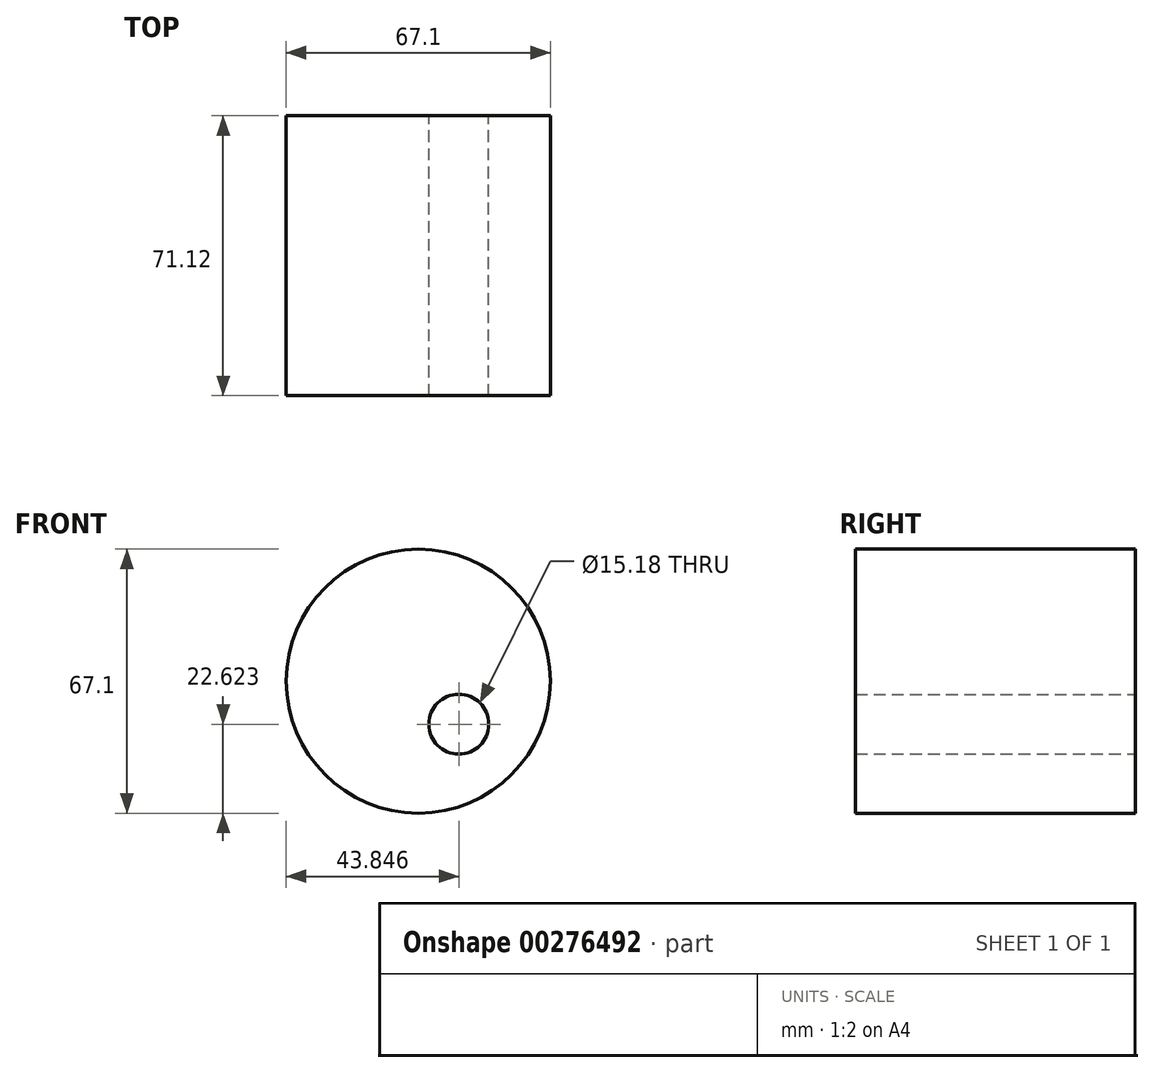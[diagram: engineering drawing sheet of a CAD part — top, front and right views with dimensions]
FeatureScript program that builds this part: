
annotation { "Feature Type Name" : "Feature", "Feature Type Description" : "" }
export const myFeature = defineFeature(function(context is Context, id is Id, definition is map)
    precondition{}
    {
        {
            var Q0;
            Q0=qCreatedBy(makeId("Front.planeOp"),FACE);
            var sketch = newSketch(context, id + "F0", { "sketchPlane" : qUnion([Q0])});
            skCircle(sketch, "E0", {"center": v(0, 0) * mm, "radius": 33.55 * mm});
            skCircle(sketch, "E1", {"center": v(10.3, -10.93) * mm, "radius": 7.6 * mm});
            skSolve(sketch);
        }
        {
            var Q0;
            Q0 = qSketchRegion(id + "F0", true);
            extrude(context, id + "F1", {"entities" : qUnion([Q0]), "depth" : 71.12 * mm});
        }
    });
